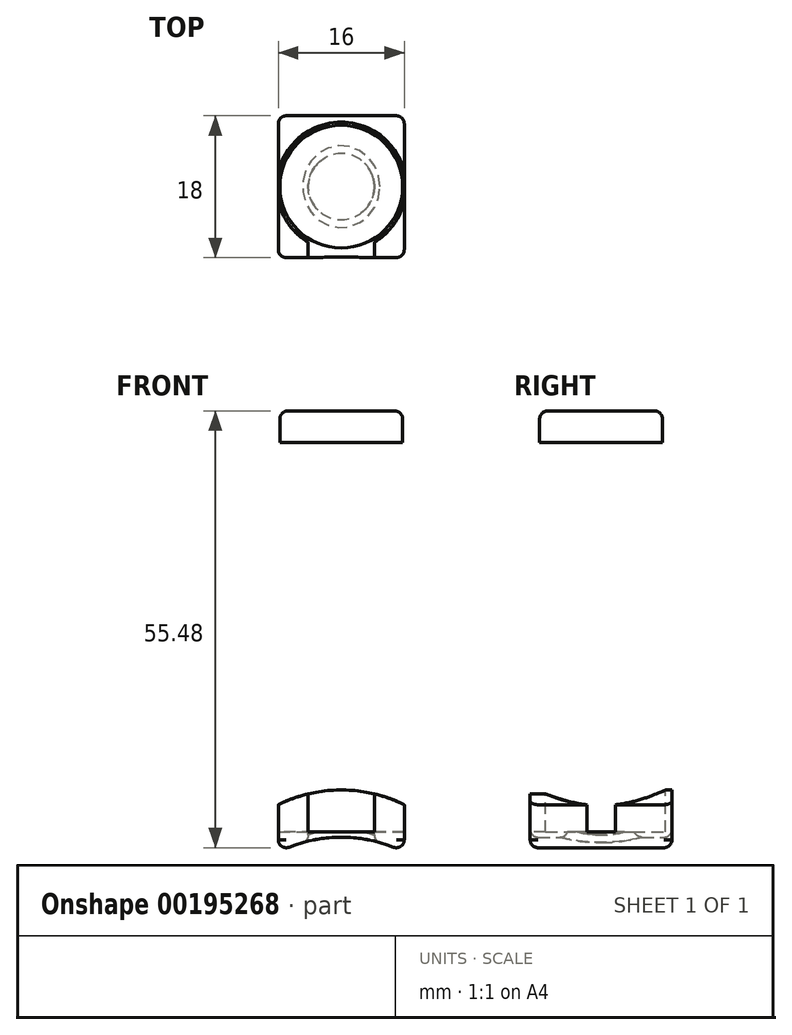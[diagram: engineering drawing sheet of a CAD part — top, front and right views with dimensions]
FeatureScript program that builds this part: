
annotation { "Feature Type Name" : "Feature", "Feature Type Description" : "" }
export const myFeature = defineFeature(function(context is Context, id is Id, definition is map)
    precondition{}
    {
        {
            var Q0;
            Q0=qCreatedBy(makeId("Front.planeOp"),FACE);
            var sketch = newSketch(context, id + "F0", { "sketchPlane" : qUnion([Q0])});
            skLineSegment(sketch, "E0.left", {"start": v(8, 2.02) * mm, "end": v(8, -2.02) * mm});
            skLineSegment(sketch, "E0.right", {"start": v(-8, 2.02) * mm, "end": v(-8, -2.02) * mm});
            skPoint(sketch, "E0.middle", {"position": v(0, 0) * mm});
            skArc(sketch, "E1", {"start": v(8, -2.02) * mm, "mid": v(0, -0.14) * mm, "end": v(-8, -2.02) * mm});
            skArc(sketch, "E2", {"start": v(8, 3.98) * mm, "mid": v(0, 5.86) * mm, "end": v(-8, 3.98) * mm});
            skLineSegment(sketch, "E3", {"start": v(-8, 2.02) * mm, "end": v(-8, 3.98) * mm});
            skLineSegment(sketch, "E4", {"start": v(8, 2.02) * mm, "end": v(8, 3.98) * mm});
            skSolve(sketch);
        }
        {
            var Q0;
            Q0 = qSketchRegion(id + "F0", true);
            extrude(context, id + "F1", {"entities" : qUnion([Q0]), "endBound" : BoundingType.SYMMETRIC, "depth" : 18 * mm});
        }
        {
            var Q0;
            Q0=qCreatedBy(makeId("Top.planeOp"),FACE);
            cPlane(context, id + "F2", {"entities" : qUnion([Q0]), "cplaneType" : CPlaneType.OFFSET, "offset" : 25 * mm, "width" : 150 * mm, "height" : 150 * mm});
        }
        {
            var Q0;
            Q0=qCreatedBy(id+"F2.planeOp",FACE);
            var sketch = newSketch(context, id + "F3", { "sketchPlane" : qUnion([Q0])});
            skCircle(sketch, "E5", {"center": v(0, 0) * mm, "radius": 4.2 * mm});
            skArc(sketch, "E6", {"start": v(4.2, -7.04) * mm, "mid": v(0, 8.2) * mm, "end": v(-4.2, -7.04) * mm});
            skLineSegment(sketch, "E7.top", {"start": v(-4.2, -9) * mm, "end": v(4.2, -9) * mm});
            skLineSegment(sketch, "E7.left", {"start": v(-4.2, -7.04) * mm, "end": v(-4.2, -9) * mm});
            skLineSegment(sketch, "E7.right", {"start": v(4.2, -7.04) * mm, "end": v(4.2, -9) * mm});
            skSolve(sketch);
        }
        {
            var Q0;
            Q0=makeQuery(id+"F3.imprint","IMPRINT",FACE,{"disambiguationData":[TD([[makeQuery(id+"F3.imprint","IMPRINT",EDGE,{"derivedFrom":sQuery(id+"F3.wireOp",EDGE,"E5")}),1.0]])]});
            extrude(context, id + "F4", {"entities" : qUnion([Q0]), "operationType" : NewBodyOperationType.REMOVE, "endBound" : BoundingType.THROUGH_ALL, "oppositeDirection" : true, "depth" : 25 * mm});
        }
        {
            var Q0;
            Q0=makeQuery(id+"F3.imprint","IMPRINT",FACE,{"disambiguationData":[TD([[makeQuery(id+"F3.imprint","IMPRINT",EDGE,{"derivedFrom":sQuery(id+"F3.wireOp",EDGE,"E5")}),-1.0]])]});
            extrude(context, id + "F5", {"entities" : qUnion([Q0]), "operationType" : NewBodyOperationType.REMOVE, "oppositeDirection" : true, "depth" : 24.5 * mm});
        }
        {
            var Q0;
            Q0=qCreatedBy(id+"F2.planeOp",FACE);
            cPlane(context, id + "F6", {"entities" : qUnion([Q0]), "cplaneType" : CPlaneType.OFFSET, "offset" : 25 * mm, "width" : 150 * mm, "height" : 150 * mm});
        }
        {
            var Q0;
            Q0=qCreatedBy(id+"F6.planeOp",FACE);
            var sketch = newSketch(context, id + "F7", { "sketchPlane" : qUnion([Q0])});
            skCircle(sketch, "E8", {"center": v(0, 0) * mm, "radius": 7.8 * mm});
            skSolve(sketch);
        }
        {
            var Q0;
            Q0=makeQuery(id+"F7.imprint","IMPRINT",FACE,{"disambiguationData":[TD([[makeQuery(id+"F7.imprint","IMPRINT",EDGE,{"derivedFrom":sQuery(id+"F7.wireOp",EDGE,"E8")}),1.0]])]});
            extrude(context, id + "F8", {"entities" : qUnion([Q0]), "depth" : 4 * mm});
        }
        {
            var Q0;
            Q0=makeQuery(id+"F1.opExtrude","CAP_EDGE",EDGE,{"disambiguationData":[OSD([sQuery(id+"F0.wireOp",EDGE,"E0.left"),sQuery(id+"F0.wireOp",EDGE,"E4")])],"isStart":false});
            var Q1;
            Q1=makeQuery(id+"F1.opExtrude","CAP_EDGE",EDGE,{"disambiguationData":[OSD([sQuery(id+"F0.wireOp",EDGE,"E0.left"),sQuery(id+"F0.wireOp",EDGE,"E4")])],"isStart":true});
            var Q2;
            Q2=makeQuery(id+"F1.opExtrude","CAP_EDGE",EDGE,{"disambiguationData":[OSD([sQuery(id+"F0.wireOp",EDGE,"E0.right"),sQuery(id+"F0.wireOp",EDGE,"E3")])],"isStart":false});
            var Q3;
            Q3=makeQuery(id+"F1.opExtrude","CAP_EDGE",EDGE,{"disambiguationData":[OSD([sQuery(id+"F0.wireOp",EDGE,"E0.right"),sQuery(id+"F0.wireOp",EDGE,"E3")])],"isStart":true});
            var Q4;
            Q4=makeQuery(id+"F8.opExtrude","CAP_EDGE",EDGE,{"disambiguationData":[OSD([sQuery(id+"F7.wireOp",EDGE,"E8")])],"isStart":false});
            fillet(context, id + "F9", {"entities" : qUnion([Q0, Q1, Q2, Q3, Q4]), "radius" : 1 * mm, "tangentPropagation" : true, "allowEdgeOverflow" : false});
        }
        {
            var Q0;
            Q0=makeQuery(id+"F1.opExtrude","SWEPT_EDGE",EDGE,{"disambiguationData":[OSD([sQuery(id+"F0.wireOp",EDGE,"E0.right"),sQuery(id+"F0.wireOp",EDGE,"E1")])]});
            var Q1;
            Q1=makeQuery(id+"F4.boolean.opBoolean","INTERSECT",EDGE,{"derivedFrom":[makeQuery(id+"F1.opExtrude","SWEPT_FACE",FACE,{"disambiguationData":[OSD([sQuery(id+"F0.wireOp",EDGE,"E1")])]}),makeQuery(id+"F4.opExtrude","SWEPT_FACE",FACE,{"disambiguationData":[OSD([sQuery(id+"F3.wireOp",EDGE,"E5")])]})]});
            fillet(context, id + "F10", {"entities" : qUnion([Q0, Q1]), "radius" : 1 * mm, "tangentPropagation" : true, "allowEdgeOverflow" : false});
        }
    });
